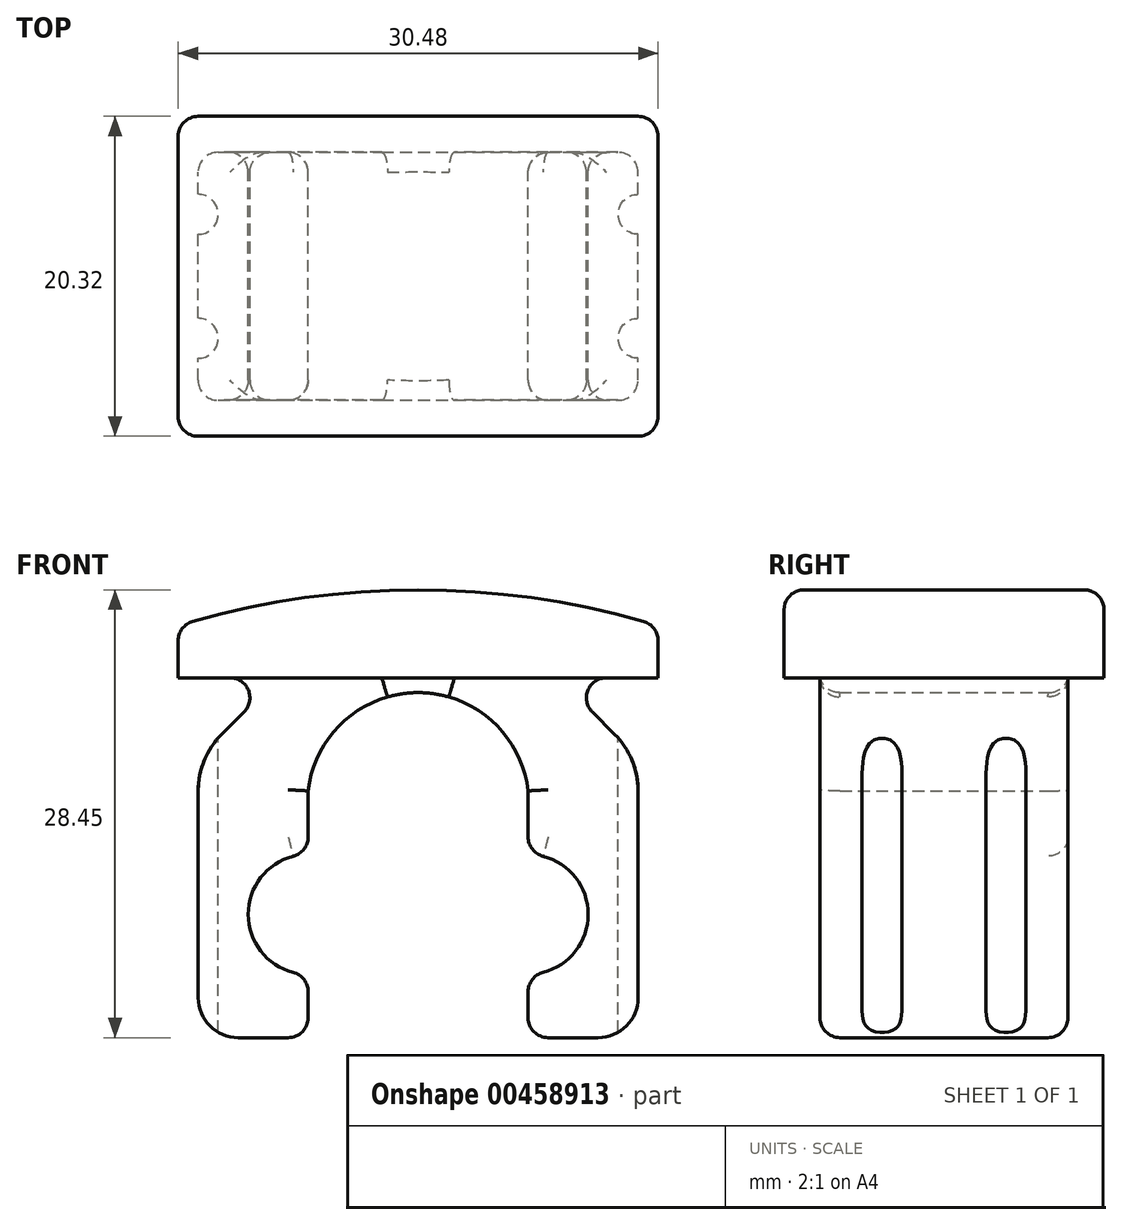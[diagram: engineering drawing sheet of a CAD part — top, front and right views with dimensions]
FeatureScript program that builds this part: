
annotation { "Feature Type Name" : "Feature", "Feature Type Description" : "" }
export const myFeature = defineFeature(function(context is Context, id is Id, definition is map)
    precondition{}
    {
        {
            var Q0;
            Q0=qCreatedBy(makeId("Front.planeOp"),FACE);
            var sketch = newSketch(context, id + "F0", { "sketchPlane" : qUnion([Q0])});
            skLineSegment(sketch, "E0", {"start": v(0, 0) * mm, "end": v(15.24, 0) * mm});
            skLineSegment(sketch, "E1", {"start": v(0, 0) * mm, "end": v(-15.24, 0) * mm});
            skLineSegment(sketch, "E2", {"start": v(0, 0) * mm, "end": v(0, 5.59) * mm});
            skLineSegment(sketch, "E3", {"start": v(-15.24, 0) * mm, "end": v(-15.24, 3.3) * mm});
            skLineSegment(sketch, "E4", {"start": v(15.24, 0) * mm, "end": v(15.24, 3.3) * mm});
            skArc(sketch, "E5", {"start": v(15.24, 3.3) * mm, "mid": v(0, 5.59) * mm, "end": v(-15.24, 3.3) * mm});
            skSolve(sketch);
        }
        {
            var Q0;
            Q0 = qSketchRegion(id + "F0", true);
            extrude(context, id + "F1", {"entities" : qUnion([Q0]), "endBound" : BoundingType.SYMMETRIC, "depth" : 20.32 * mm});
        }
        {
            var Q0;
            Q0=qCreatedBy(makeId("Front.planeOp"),FACE);
            var sketch = newSketch(context, id + "F2", { "sketchPlane" : qUnion([Q0])});
            skPoint(sketch, "E6.0", {"position": v(-15.24, 0) * mm});
            skLineSegment(sketch, "E7", {"start": v(-15.24, 0) * mm, "end": v(-13.97, 0) * mm});
            skLineSegment(sketch, "E8", {"start": v(-13.97, -7.18) * mm, "end": v(-13.97, -20.32) * mm});
            skLineSegment(sketch, "E9", {"start": v(0, 0) * mm, "end": v(0, -22.86) * mm, "construction": true});
            skLineSegment(sketch, "E10", {"start": v(-11.43, -22.86) * mm, "end": v(-8.25, -22.86) * mm});
            skPoint(sketch, "E11.end.orphan", {"position": v(13.97, 0) * mm});
            skPoint(sketch, "E12.end.orphan", {"position": v(13.97, -22.86) * mm});
            skLineSegment(sketch, "E13", {"start": v(-13.97, 0) * mm, "end": v(-11.96, 0) * mm});
            skLineSegment(sketch, "E14", {"start": v(-11.06, -2.17) * mm, "end": v(-12.48, -3.6) * mm});
            skLineSegment(sketch, "E15", {"start": v(-6.98, -21.59) * mm, "end": v(-6.98, -19.94) * mm});
            skPoint(sketch, "E16.visualSharp", {"position": v(-8.89, 0) * mm});
            skArc(sketch, "E16.filletArc", {"start": v(-11.06, -2.17) * mm, "mid": v(-10.78, -0.78) * mm, "end": v(-11.96, 0) * mm});
            skPoint(sketch, "E17.visualSharp", {"position": v(-13.97, -5.08) * mm});
            skArc(sketch, "E17.filletArc", {"start": v(-12.48, -3.6) * mm, "mid": v(-13.58, -5.24) * mm, "end": v(-13.97, -7.18) * mm});
            skPoint(sketch, "E18.visualSharp", {"position": v(-6.98, -5.08) * mm});
            skArc(sketch, "E19", {"start": v(-7.94, -11.33) * mm, "mid": v(-10.8, -15.02) * mm, "end": v(-7.94, -18.71) * mm});
            skLineSegment(sketch, "E20.trimOffspring", {"start": v(-6.98, -10.1) * mm, "end": v(-6.98, -7.18) * mm});
            skPoint(sketch, "E21.end.orphan", {"position": v(0, -15.02) * mm});
            skPoint(sketch, "E22.visualSharp", {"position": v(-13.97, -22.86) * mm});
            skArc(sketch, "E22.filletArc", {"start": v(-13.97, -20.32) * mm, "mid": v(-13.23, -22.12) * mm, "end": v(-11.43, -22.86) * mm});
            skPoint(sketch, "E23.visualSharp", {"position": v(-6.98, -22.86) * mm});
            skArc(sketch, "E23.filletArc", {"start": v(-8.25, -22.86) * mm, "mid": v(-7.36, -22.49) * mm, "end": v(-6.98, -21.59) * mm});
            skPoint(sketch, "E24.visualSharp", {"position": v(-6.98, -11.21) * mm});
            skArc(sketch, "E24.filletArc", {"start": v(-7.94, -11.33) * mm, "mid": v(-7.25, -10.88) * mm, "end": v(-6.98, -10.1) * mm});
            skPoint(sketch, "E25.visualSharp", {"position": v(-6.98, -18.83) * mm});
            skArc(sketch, "E25.filletArc", {"start": v(-6.98, -19.94) * mm, "mid": v(-7.25, -19.16) * mm, "end": v(-7.94, -18.71) * mm});
            skPoint(sketch, "E26.end.orphan", {"position": v(-1.9, 0) * mm});
            skLineSegment(sketch, "E27.MirrorCS", {"start": v(6.99, -21.59) * mm, "end": v(6.99, -19.94) * mm});
            skLineSegment(sketch, "E28.MirrorCS", {"start": v(11.06, -2.17) * mm, "end": v(12.48, -3.6) * mm});
            skLineSegment(sketch, "E29.MirrorCS", {"start": v(15.24, 0) * mm, "end": v(13.97, 0) * mm});
            skArc(sketch, "E30.MirrorCS", {"start": v(6.99, -19.94) * mm, "mid": v(7.25, -19.16) * mm, "end": v(7.94, -18.71) * mm});
            skArc(sketch, "E31.MirrorCS", {"start": v(7.94, -11.33) * mm, "mid": v(7.25, -10.88) * mm, "end": v(6.98, -10.1) * mm});
            skArc(sketch, "E32.MirrorCS", {"start": v(11.06, -2.17) * mm, "mid": v(10.78, -0.78) * mm, "end": v(11.96, 0) * mm});
            skArc(sketch, "E33.MirrorCS", {"start": v(12.48, -3.6) * mm, "mid": v(13.58, -5.24) * mm, "end": v(13.97, -7.18) * mm});
            skArc(sketch, "E34.MirrorCS", {"start": v(8.26, -22.86) * mm, "mid": v(7.36, -22.49) * mm, "end": v(6.99, -21.59) * mm});
            skLineSegment(sketch, "E35.MirrorCS", {"start": v(13.97, 0) * mm, "end": v(11.96, 0) * mm});
            skLineSegment(sketch, "E36.MirrorCS", {"start": v(11.43, -22.86) * mm, "end": v(8.26, -22.86) * mm});
            skLineSegment(sketch, "E37.MirrorCS", {"start": v(13.97, -7.18) * mm, "end": v(13.97, -20.32) * mm});
            skPoint(sketch, "E38.MirrorP", {"position": v(15.24, 0) * mm});
            skPoint(sketch, "E39.MirrorP", {"position": v(6.99, -22.86) * mm});
            skPoint(sketch, "E40.MirrorP", {"position": v(6.99, -18.83) * mm});
            skPoint(sketch, "E41.MirrorP", {"position": v(8.89, 0) * mm});
            skPoint(sketch, "E42.MirrorP", {"position": v(13.97, -5.08) * mm});
            skPoint(sketch, "E43.MirrorP", {"position": v(6.98, -5.08) * mm});
            skArc(sketch, "E44.MirrorCS", {"start": v(13.97, -20.32) * mm, "mid": v(13.23, -22.12) * mm, "end": v(11.43, -22.86) * mm});
            skLineSegment(sketch, "E45.MirrorCS", {"start": v(6.99, -10.1) * mm, "end": v(6.98, -7.18) * mm});
            skPoint(sketch, "E46.MirrorP", {"position": v(6.99, -11.21) * mm});
            skArc(sketch, "E47.MirrorCS", {"start": v(7.94, -11.33) * mm, "mid": v(10.8, -15.02) * mm, "end": v(7.94, -18.71) * mm});
            skLineSegment(sketch, "E48", {"start": v(-15.24, 0) * mm, "end": v(15.24, 0) * mm});
            skArc(sketch, "E49", {"start": v(6.98, -7.18) * mm, "mid": v(0, -0.94) * mm, "end": v(-6.98, -7.18) * mm});
            skPoint(sketch, "E50.end.orphan", {"position": v(-5.5, 0) * mm});
            skPoint(sketch, "E50.start.orphan", {"position": v(-5.5, -3.6) * mm});
            skPoint(sketch, "E51.MirrorCS.end.orphan", {"position": v(5.5, 0) * mm});
            skPoint(sketch, "E51.MirrorCS.start.orphan", {"position": v(5.5, -3.6) * mm});
            skSolve(sketch);
        }
        {
            var Q0;
            Q0 = qSketchRegion(id + "F2", true);
            extrude(context, id + "F3", {"entities" : qUnion([Q0]), "operationType" : NewBodyOperationType.ADD, "endBound" : BoundingType.SYMMETRIC, "depth" : 15.75 * mm});
        }
        {
            var Q0;
            Q0=makeQuery(id+"F1.opExtrude","CAP_EDGE",EDGE,{"disambiguationData":[OSD([sQuery(id+"F0.wireOp",EDGE,"E5")])],"isStart":true});
            var Q1;
            Q1=makeQuery(id+"F1.opExtrude","CAP_EDGE",EDGE,{"disambiguationData":[OSD([sQuery(id+"F0.wireOp",EDGE,"E5")])],"isStart":false});
            var Q2;
            Q2=makeQuery(id+"F1.opExtrude","SWEPT_EDGE",EDGE,{"disambiguationData":[OSD([sQuery(id+"F0.wireOp",EDGE,"E4"),sQuery(id+"F0.wireOp",EDGE,"E5")])]});
            var Q3;
            Q3=makeQuery(id+"F1.opExtrude","CAP_EDGE",EDGE,{"disambiguationData":[OSD([sQuery(id+"F0.wireOp",EDGE,"E4")])],"isStart":false});
            var Q4;
            Q4=makeQuery(id+"F1.opExtrude","CAP_EDGE",EDGE,{"disambiguationData":[OSD([sQuery(id+"F0.wireOp",EDGE,"E4")])],"isStart":true});
            var Q5;
            Q5=makeQuery(id+"F1.opExtrude","CAP_EDGE",EDGE,{"disambiguationData":[OSD([sQuery(id+"F0.wireOp",EDGE,"E3")])],"isStart":true});
            var Q6;
            Q6=makeQuery(id+"F1.opExtrude","CAP_EDGE",EDGE,{"disambiguationData":[OSD([sQuery(id+"F0.wireOp",EDGE,"E3")])],"isStart":false});
            var Q7;
            Q7=makeQuery(id+"F1.opExtrude","SWEPT_EDGE",EDGE,{"disambiguationData":[OSD([sQuery(id+"F0.wireOp",EDGE,"E3"),sQuery(id+"F0.wireOp",EDGE,"E5")])]});
            fillet(context, id + "F4", {"entities" : qUnion([Q0, Q1, Q2, Q3, Q4, Q5, Q6, Q7]), "radius" : 1.27 * mm, "tangentPropagation" : true, "allowEdgeOverflow" : false});
        }
        {
            var Q0;
            Q0=makeQuery(id+"F1.opExtrude","SWEPT_FACE",FACE,{"disambiguationData":[OSD([sQuery(id+"F0.wireOp",EDGE,"E0"),sQuery(id+"F0.wireOp",EDGE,"E1")])]});
            var sketch = newSketch(context, id + "F5", { "sketchPlane" : qUnion([Q0])});
            skPoint(sketch, "E52.0", {"position": v(-13.97, 0) * mm});
            skPoint(sketch, "E53.0", {"position": v(13.97, 0) * mm});
            skPoint(sketch, "E54.0", {"position": v(-13.97, -7.87) * mm});
            skPoint(sketch, "E55.0", {"position": v(-13.97, 7.87) * mm});
            skPoint(sketch, "E56.0", {"position": v(13.97, 7.87) * mm});
            skPoint(sketch, "E57.0", {"position": v(13.97, -7.87) * mm});
            skLineSegment(sketch, "E58", {"start": v(-13.97, 7.87) * mm, "end": v(-13.97, 5.2) * mm});
            skLineSegment(sketch, "E59", {"start": v(13.97, 7.87) * mm, "end": v(13.97, 5.2) * mm});
            skLineSegment(sketch, "E60", {"start": v(13.97, -7.87) * mm, "end": v(13.97, -5.2) * mm});
            skCircle(sketch, "E61", {"center": v(-13.97, -3.94) * mm, "radius": 1.27 * mm});
            skCircle(sketch, "E62", {"center": v(-13.97, 3.94) * mm, "radius": 1.27 * mm});
            skCircle(sketch, "E63", {"center": v(13.97, 3.94) * mm, "radius": 1.27 * mm});
            skCircle(sketch, "E64", {"center": v(13.97, -3.94) * mm, "radius": 1.27 * mm});
            skLineSegment(sketch, "E65.trimOffspring", {"start": v(-13.97, -2.67) * mm, "end": v(-13.97, 0) * mm});
            skLineSegment(sketch, "E66.trimOffspring", {"start": v(-13.97, 2.67) * mm, "end": v(-13.97, 0) * mm});
            skLineSegment(sketch, "E67.trimOffspring", {"start": v(13.97, 2.67) * mm, "end": v(13.97, 0) * mm});
            skLineSegment(sketch, "E68.trimOffspring", {"start": v(13.97, -2.67) * mm, "end": v(13.97, 0) * mm});
            skSolve(sketch);
        }
        {
            var Q0;
            Q0 = qSketchRegion(id + "F5", true);
            extrude(context, id + "F6", {"entities" : qUnion([Q0]), "operationType" : NewBodyOperationType.REMOVE, "depth" : 25.1 * mm});
        }
        {
            var Q0;
            Q0=makeQuery(id+"F3.opExtrude","CAP_EDGE",EDGE,{"disambiguationData":[OSD([sQuery(id+"F2.wireOp",EDGE,"E49")])],"isStart":false});
            var Q1;
            Q1=makeQuery(id+"F3.opExtrude","CAP_EDGE",EDGE,{"disambiguationData":[OSD([sQuery(id+"F2.wireOp",EDGE,"E20.trimOffspring")])],"isStart":false});
            var Q2;
            Q2=makeQuery(id+"F3.opExtrude","CAP_EDGE",EDGE,{"disambiguationData":[OSD([sQuery(id+"F2.wireOp",EDGE,"E24.filletArc")])],"isStart":false});
            var Q3;
            Q3=makeQuery(id+"F3.opExtrude","CAP_EDGE",EDGE,{"disambiguationData":[OSD([sQuery(id+"F2.wireOp",EDGE,"E19")])],"isStart":false});
            var Q4;
            Q4=makeQuery(id+"F3.opExtrude","CAP_EDGE",EDGE,{"disambiguationData":[OSD([sQuery(id+"F2.wireOp",EDGE,"E25.filletArc")])],"isStart":false});
            var Q5;
            Q5=makeQuery(id+"F3.opExtrude","CAP_EDGE",EDGE,{"disambiguationData":[OSD([sQuery(id+"F2.wireOp",EDGE,"E15")])],"isStart":false});
            var Q6;
            Q6=makeQuery(id+"F3.opExtrude","CAP_EDGE",EDGE,{"disambiguationData":[OSD([sQuery(id+"F2.wireOp",EDGE,"E23.filletArc")])],"isStart":false});
            var Q7;
            Q7=makeQuery(id+"F3.opExtrude","CAP_EDGE",EDGE,{"disambiguationData":[OSD([sQuery(id+"F2.wireOp",EDGE,"E31.MirrorCS")])],"isStart":false});
            var Q8;
            Q8=makeQuery(id+"F3.opExtrude","CAP_EDGE",EDGE,{"disambiguationData":[OSD([sQuery(id+"F2.wireOp",EDGE,"E47.MirrorCS")])],"isStart":true});
            var Q9;
            Q9=makeQuery(id+"F3.opExtrude","CAP_EDGE",EDGE,{"disambiguationData":[OSD([sQuery(id+"F2.wireOp",EDGE,"E19")])],"isStart":true});
            fillet(context, id + "F7", {"entities" : qUnion([Q0, Q1, Q2, Q3, Q4, Q5, Q6, Q7, Q8, Q9]), "radius" : 1.27 * mm, "tangentPropagation" : true, "allowEdgeOverflow" : false});
        }
        {
            var Q0;
            Q0=makeQuery(id+"F3.opExtrude","CAP_EDGE",EDGE,{"disambiguationData":[OSD([sQuery(id+"F2.wireOp",EDGE,"E49")])],"isStart":true});
            var Q1;
            Q1=makeQuery(id+"F3.opExtrude","CAP_EDGE",EDGE,{"disambiguationData":[OSD([sQuery(id+"F2.wireOp",EDGE,"E45.MirrorCS")])],"isStart":true});
            var Q2;
            Q2=makeQuery(id+"F3.opExtrude","CAP_EDGE",EDGE,{"disambiguationData":[OSD([sQuery(id+"F2.wireOp",EDGE,"E20.trimOffspring")])],"isStart":true});
            fillet(context, id + "F8", {"entities" : qUnion([Q0, Q1, Q2]), "radius" : 1.27 * mm, "tangentPropagation" : true, "allowEdgeOverflow" : false});
        }
    });
